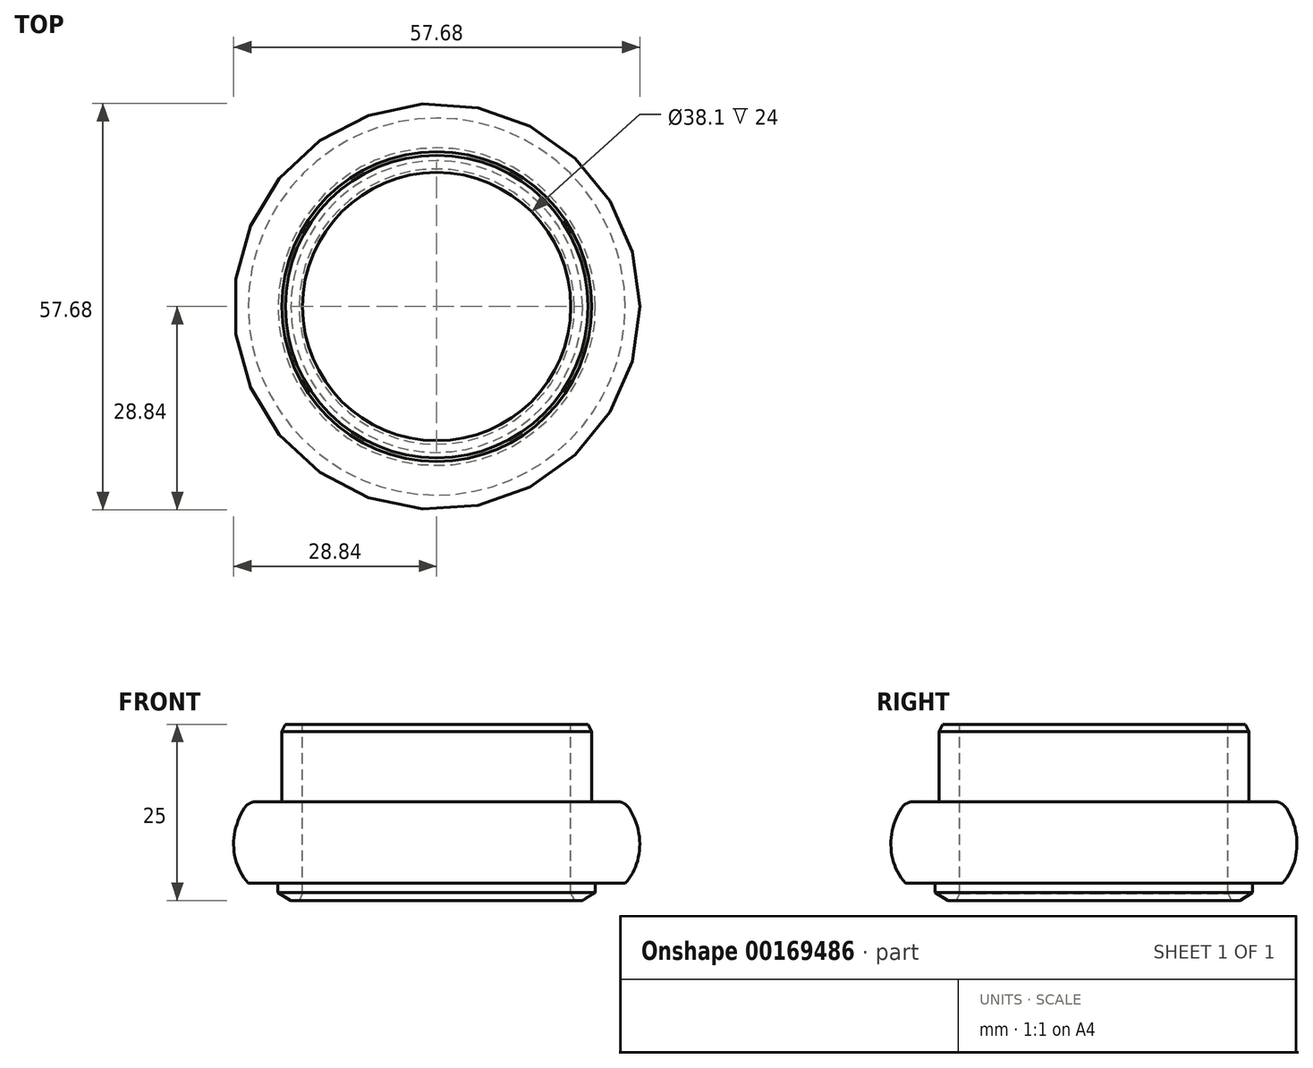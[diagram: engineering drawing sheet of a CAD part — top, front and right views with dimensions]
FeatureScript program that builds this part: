
annotation { "Feature Type Name" : "Feature", "Feature Type Description" : "" }
export const myFeature = defineFeature(function(context is Context, id is Id, definition is map)
    precondition{}
    {
        {
            var Q0;
            Q0=qCreatedBy(makeId("Front.planeOp"),FACE);
            var sketch = newSketch(context, id + "F0", { "sketchPlane" : qUnion([Q0])});
            skLineSegment(sketch, "E0", {"start": v(0, 0) * mm, "end": v(-22, 0) * mm, "construction": true});
            skLineSegment(sketch, "E1", {"start": v(-22, 0) * mm, "end": v(-22, -10.96) * mm});
            skLineSegment(sketch, "E2", {"start": v(-22, -10.96) * mm, "end": v(-26.66, -10.96) * mm});
            skLineSegment(sketch, "E3", {"start": v(0, -25) * mm, "end": v(-19.05, -25) * mm, "construction": true});
            skLineSegment(sketch, "E4", {"start": v(-19.05, -25) * mm, "end": v(-19.05, 0) * mm});
            skLineSegment(sketch, "E5", {"start": v(0, -32.42) * mm, "end": v(-19.9, -32.42) * mm, "construction": true});
            skLineSegment(sketch, "E6", {"start": v(-19.05, -25) * mm, "end": v(-20.71, -25) * mm});
            skPoint(sketch, "E7.endSnap0", {"position": v(-22, -5.48) * mm});
            skLineSegment(sketch, "E8", {"start": v(-22.54, -22.55) * mm, "end": v(-26.77, -22.55) * mm});
            skFitSpline(sketch, "E9", {"points": [v(-26.66, -10.96) * mm, v(-26.77, -22.55) * mm], "startDerivative": vector(-9.35, -11.88) * mm, "endDerivative": vector(7.6, -8.2) * mm});
            skLineSegment(sketch, "E10", {"start": v(-22.54, -22.55) * mm, "end": v(-22.54, -23.88) * mm});
            skLineSegment(sketch, "E11", {"start": v(-22.54, -23.88) * mm, "end": v(-20.71, -25) * mm});
            skLineSegment(sketch, "E12", {"start": v(-22, 0) * mm, "end": v(-19.05, 0) * mm});
            skLineSegment(sketch, "E13", {"start": v(0, 0) * mm, "end": v(0, -25) * mm, "construction": true});
            skSolve(sketch);
        }
        {
            var Q0;
            Q0=makeQuery(id+"F0.imprint","IMPRINT",FACE,{"disambiguationData":[TD([[makeQuery(id+"F0.imprint","IMPRINT",EDGE,{"derivedFrom":sQuery(id+"F0.wireOp",EDGE,"E1")}),1.0]])]});
            var Q1;
            Q1=sQuery(id+"F0.wireOp",EDGE,"E13");
            revolve(context, id + "F1", {"entities" : qUnion([Q0]), "axis" : qUnion([Q1]), "revolveType" : RevolveType.FULL});
        }
        {
            var Q0;
            Q0=makeQuery(id+"F1.opRevolve","SWEPT_EDGE",EDGE,{"disambiguationData":[OSD([sQuery(id+"F0.wireOp",EDGE,"E2"),sQuery(id+"F0.wireOp",EDGE,"E9")])]});
            fillet(context, id + "F2", {"entities" : qUnion([Q0]), "radius" : 2 * mm, "tangentPropagation" : true, "allowEdgeOverflow" : false});
        }
        {
            var Q0;
            Q0=makeQuery(id+"F1.opRevolve","SWEPT_EDGE",EDGE,{"disambiguationData":[OSD([sQuery(id+"F0.wireOp",EDGE,"E1"),sQuery(id+"F0.wireOp",EDGE,"E12")])]});
            var Q1;
            Q1=makeQuery(id+"F1.opRevolve","SWEPT_EDGE",EDGE,{"disambiguationData":[OSD([sQuery(id+"F0.wireOp",EDGE,"E4"),sQuery(id+"F0.wireOp",EDGE,"E6")])]});
            chamfer(context, id + "F3", {"entities" : qUnion([Q0, Q1]), "chamferType" : ChamferType.TWO_OFFSETS, "width1" : 0.5 * mm, "oppositeDirection" : false, "width2" : 1 * mm, "tangentPropagation" : true});
        }
    });
